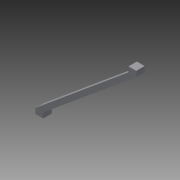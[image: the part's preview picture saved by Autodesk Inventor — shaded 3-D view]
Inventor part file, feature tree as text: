
AUTODESK INVENTOR PART (.ipt)
format: ipt  version: 2013 (Build 170138000, 138)  size: 75,776 bytes
history: native  units: in
note: dims shown in document units (in); Inventor stores cm internally (conversion verified against a paired STEP export)
features: extrude x1, sketch x1
ambient origin geometry x8: Origin, YZ Plane, XZ Plane, XY Plane, X Axis, Y Axis, Z Axis, Center Point
bodies: Solid1 (feature_tree)
feature tree (2):
  extrude  "Extrusion1"  Depth=0.25in
  sketch  "Sketch1"  dims[d0=0.375in d1=0.25in d2=0.25in d3=0.375in d4=4.088in d6=0.25in d7=0.4in d8=0.0in d10=0.25in d11=3.707in]
